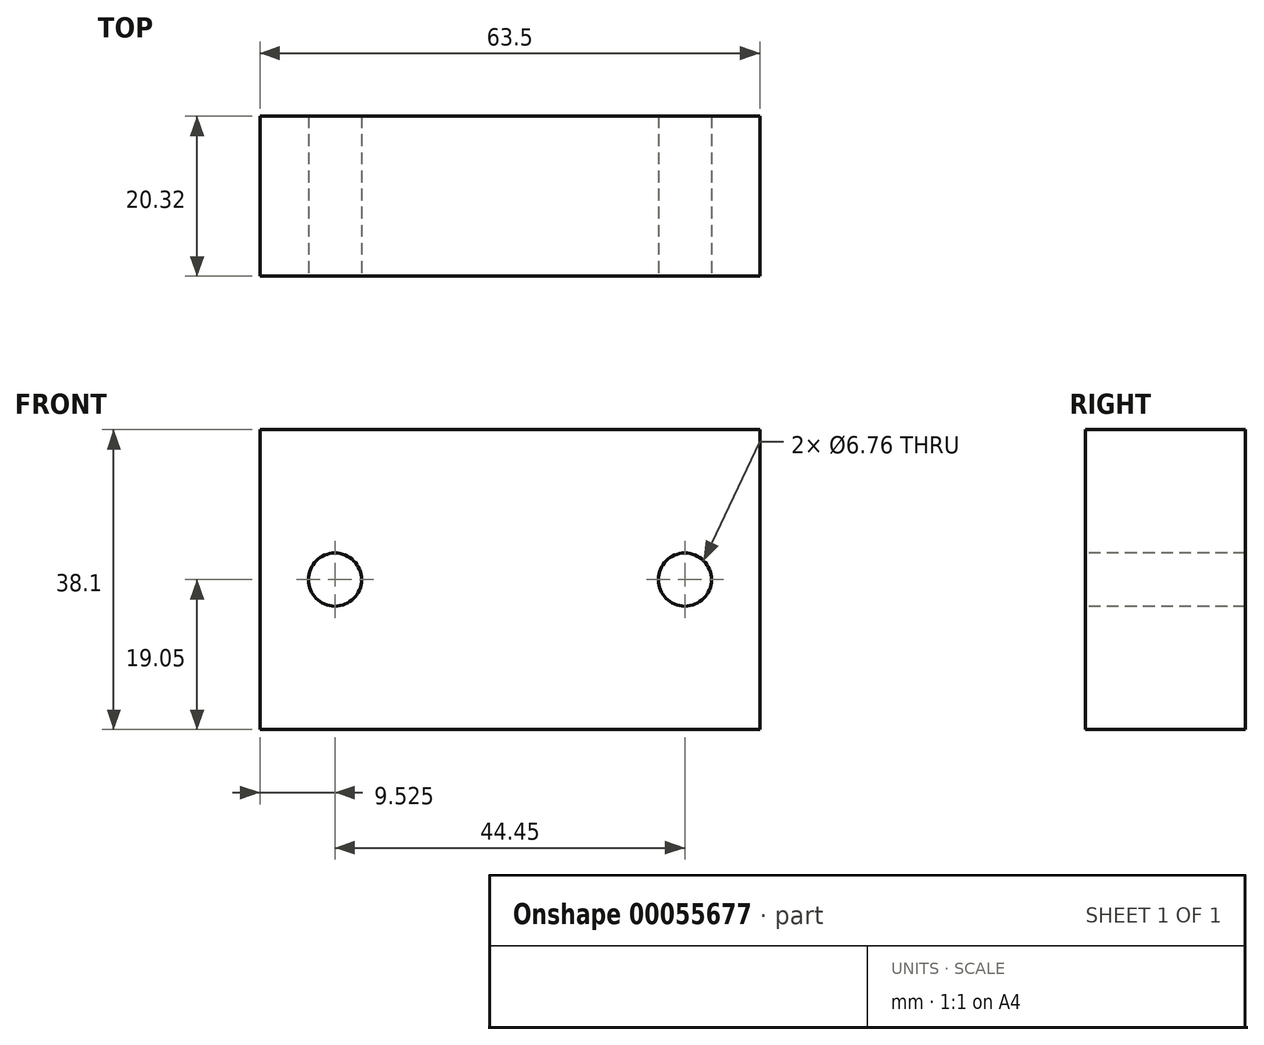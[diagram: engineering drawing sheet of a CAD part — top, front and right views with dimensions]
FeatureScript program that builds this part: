
annotation { "Feature Type Name" : "Feature", "Feature Type Description" : "" }
export const myFeature = defineFeature(function(context is Context, id is Id, definition is map)
    precondition{}
    {
        {
            var Q0;
            Q0=qCreatedBy(makeId("Front.planeOp"),FACE);
            var sketch = newSketch(context, id + "F0", { "sketchPlane" : qUnion([Q0])});
            skLineSegment(sketch, "E0.bottom", {"start": v(0, 0) * mm, "end": v(63.5, 0) * mm});
            skLineSegment(sketch, "E0.top", {"start": v(0, 38.1) * mm, "end": v(63.5, 38.1) * mm});
            skLineSegment(sketch, "E0.left", {"start": v(0, 0) * mm, "end": v(0, 38.1) * mm});
            skLineSegment(sketch, "E0.right", {"start": v(63.5, 0) * mm, "end": v(63.5, 38.1) * mm});
            skSolve(sketch);
        }
        {
            var Q0;
            Q0 = qSketchRegion(id + "F0", true);
            extrude(context, id + "F1", {"entities" : qUnion([Q0]), "oppositeDirection" : true, "depth" : 20.32 * mm});
        }
        {
            var Q0;
            Q0=makeQuery(id+"F1.opExtrude","CAP_FACE",FACE,{"disambiguationData":[OSD([sQuery(id+"F0.wireOp",EDGE,"E0.bottom"),sQuery(id+"F0.wireOp",EDGE,"E0.top"),sQuery(id+"F0.wireOp",EDGE,"E0.left"),sQuery(id+"F0.wireOp",EDGE,"E0.right")])],"isStart":true});
            var sketch = newSketch(context, id + "F2", { "sketchPlane" : qUnion([Q0])});
            skLineSegment(sketch, "E1", {"start": v(0, 19.05) * mm, "end": v(63.5, 19.05) * mm});
            skPoint(sketch, "E2", {"position": v(9.53, 19.05) * mm});
            skPoint(sketch, "E3", {"position": v(53.98, 19.05) * mm});
            skSolve(sketch);
        }
        {
            var Q0;
            Q0=sQuery(id+"F2.wireOp",VERTEX,"E2");
            var Q1;
            Q1=sQuery(id+"F2.wireOp",VERTEX,"E3");
            var Q2;
            Q2=makeQuery(id+"F1.opExtrude","SWEPT_BODY",BODY,{"disambiguationData":[OSD([sQuery(id+"F0.wireOp",EDGE,"E0.bottom"),sQuery(id+"F0.wireOp",EDGE,"E0.top"),sQuery(id+"F0.wireOp",EDGE,"E0.left"),sQuery(id+"F0.wireOp",EDGE,"E0.right")])]});
            hole(context, id + "F3", {"style" : HoleStyle.SIMPLE, "holeDiameter" : 6.76 * mm, "endStyle" : HoleEndStyle.THROUGH, "locations" : qUnion([Q0, Q1]), "scope" : qUnion([Q2])});
        }
    });
